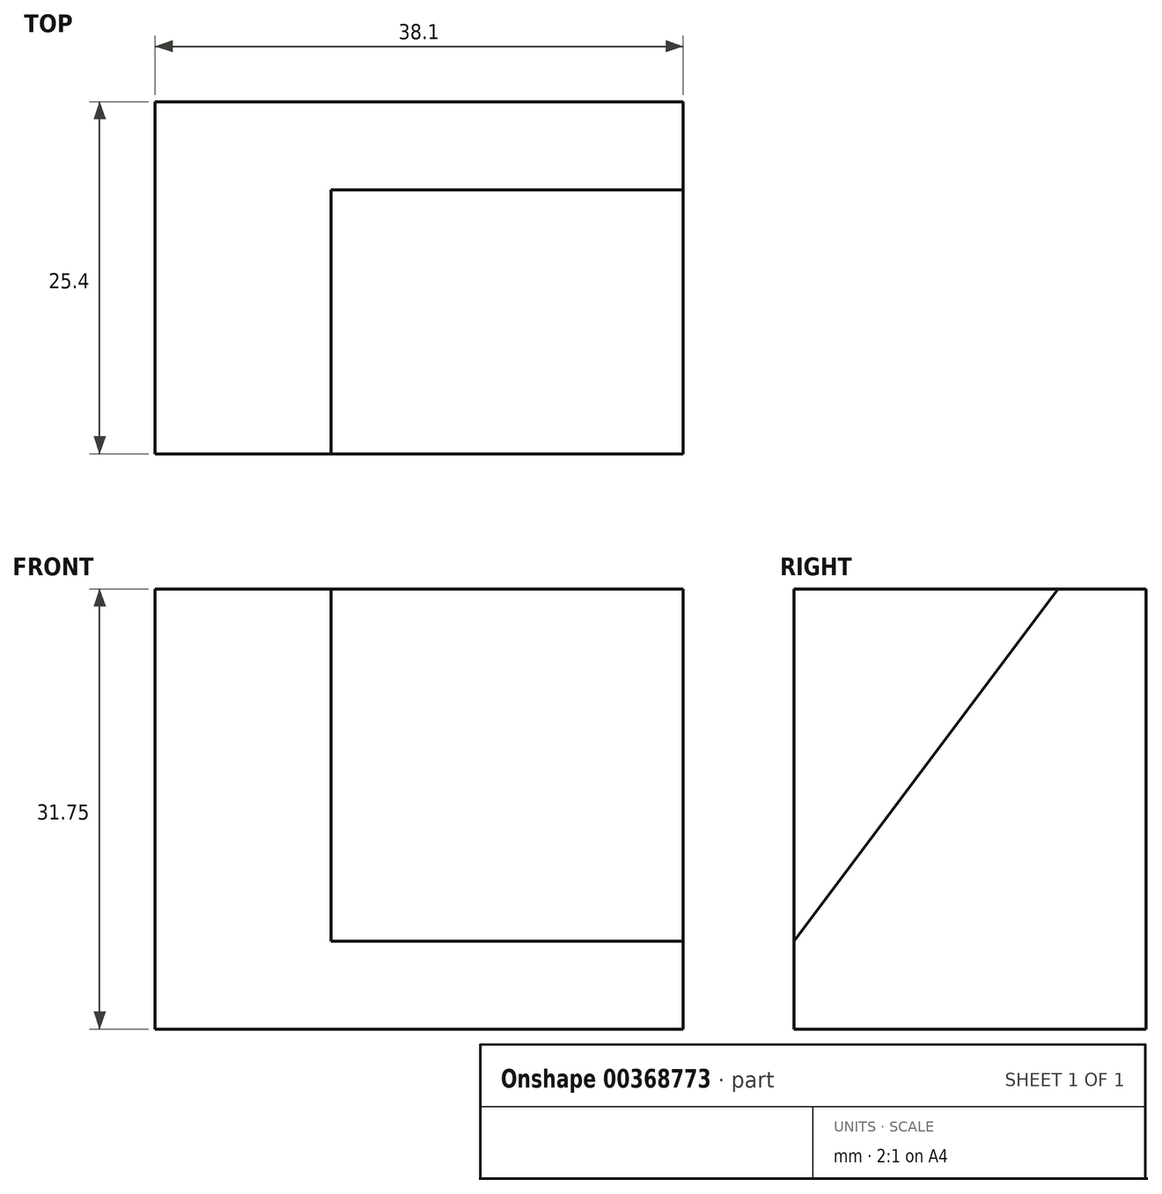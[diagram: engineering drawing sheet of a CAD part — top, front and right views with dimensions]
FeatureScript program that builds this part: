
annotation { "Feature Type Name" : "Feature", "Feature Type Description" : "" }
export const myFeature = defineFeature(function(context is Context, id is Id, definition is map)
    precondition{}
    {
        {
            var Q0;
            Q0=qCreatedBy(makeId("Top.planeOp"),FACE);
            var sketch = newSketch(context, id + "F0", { "sketchPlane" : qUnion([Q0])});
            skLineSegment(sketch, "E0", {"start": v(0, 0) * mm, "end": v(0, 25.4) * mm});
            skLineSegment(sketch, "E1", {"start": v(0, 25.4) * mm, "end": v(38.1, 25.4) * mm});
            skLineSegment(sketch, "E2", {"start": v(38.1, 25.4) * mm, "end": v(38.1, 19.05) * mm});
            skLineSegment(sketch, "E3", {"start": v(38.1, 19.05) * mm, "end": v(12.7, 19.05) * mm});
            skLineSegment(sketch, "E4", {"start": v(12.7, 19.05) * mm, "end": v(12.7, 0) * mm});
            skLineSegment(sketch, "E5", {"start": v(12.7, 0) * mm, "end": v(0, 0) * mm});
            skSolve(sketch);
        }
        {
            var Q0;
            Q0 = qSketchRegion(id + "F0", true);
            extrude(context, id + "F1", {"entities" : qUnion([Q0]), "depth" : 31.75 * mm});
        }
        {
            var Q0;
            Q0=makeQuery(id+"F1.opExtrude","SWEPT_FACE",FACE,{"disambiguationData":[OSD([sQuery(id+"F0.wireOp",EDGE,"E4")])]});
            var sketch = newSketch(context, id + "F2", { "sketchPlane" : qUnion([Q0])});
            skLineSegment(sketch, "E6", {"start": v(0, 0) * mm, "end": v(0, 6.35) * mm});
            skLineSegment(sketch, "E7", {"start": v(0, 6.35) * mm, "end": v(19.05, 31.75) * mm});
            skSolve(sketch);
        }
        {
            var Q0;
            Q0 = qSketchRegion(id + "F2", true);
            var Q1;
            Q1=makeQuery(id+"F2.imprint","IMPRINT",FACE,{"disambiguationData":[TD([[makeQuery(id+"F2.imprint","IMPRINT",EDGE,{"derivedFrom":sQuery(id+"F2.wireOp",EDGE,"E6")}),1.0]])]});
            extrude(context, id + "F3", {"entities" : qUnion([Q0, Q1]), "operationType" : NewBodyOperationType.ADD, "depth" : 25.4 * mm});
        }
    });
